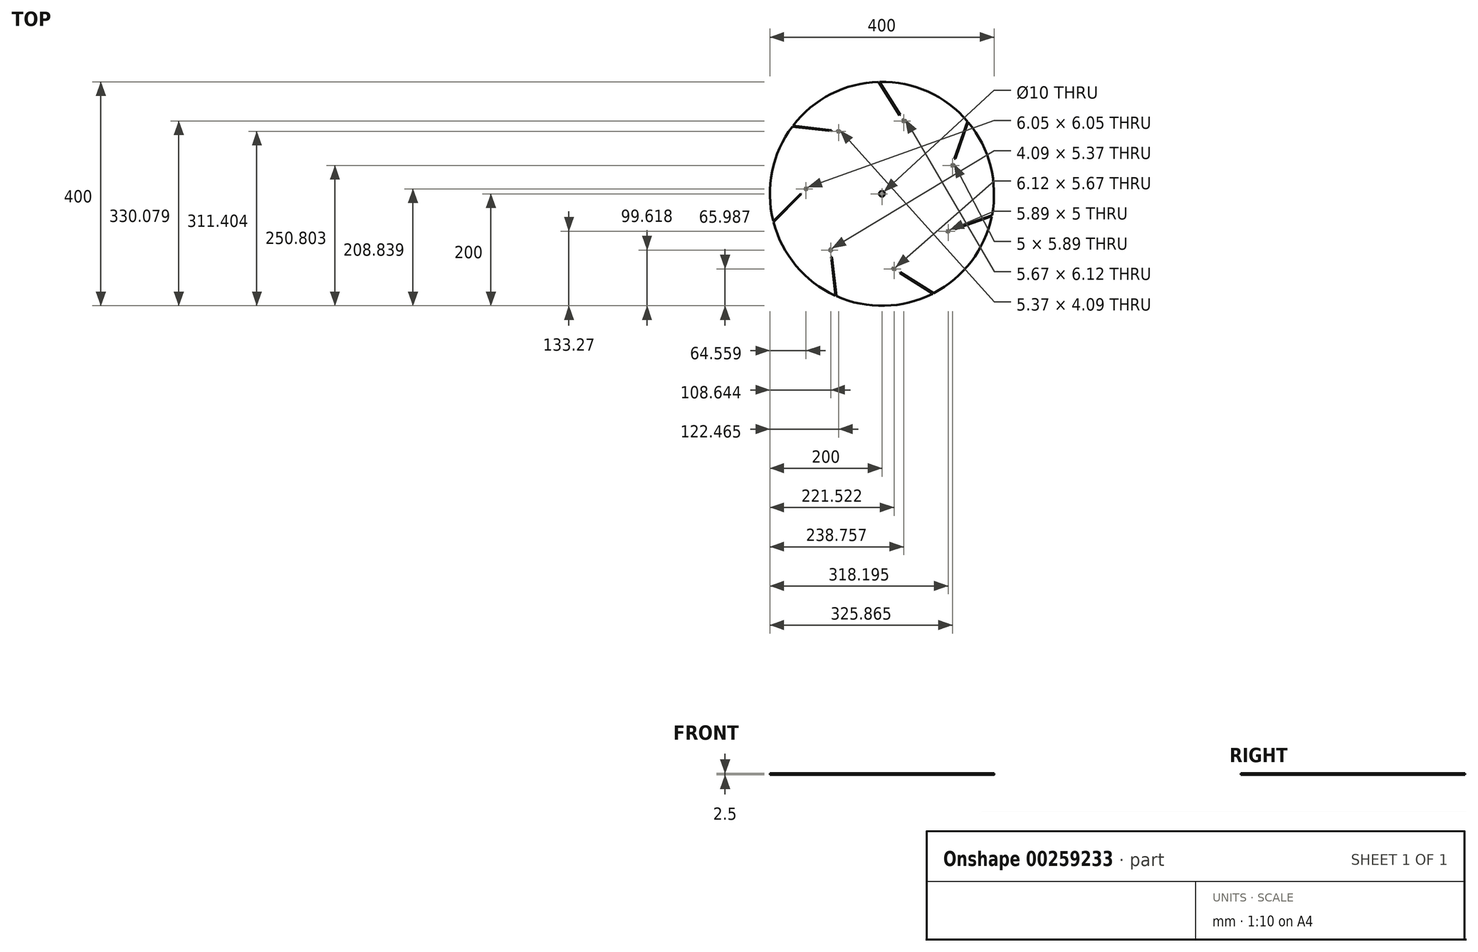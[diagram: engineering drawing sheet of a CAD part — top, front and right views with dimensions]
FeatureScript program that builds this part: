
annotation { "Feature Type Name" : "Feature", "Feature Type Description" : "" }
export const myFeature = defineFeature(function(context is Context, id is Id, definition is map)
    precondition{}
    {
        {
            var Q0;
            Q0=qCreatedBy(makeId("Top.planeOp"),FACE);
            var sketch = newSketch(context, id + "F0", { "sketchPlane" : qUnion([Q0])});
            skLineSegment(sketch, "E0", {"start": v(40, 0) * mm, "end": v(-285.91, 0) * mm, "construction": true});
            skCircle(sketch, "E1", {"center": v(0, 0) * mm, "radius": 70 * mm, "construction": true});
            skLineSegment(sketch, "E2", {"start": v(-49.5, -49.5) * mm, "end": v(49.5, 49.5) * mm, "construction": true});
            skLineSegment(sketch, "E3", {"start": v(-49.5, -49.5) * mm, "end": v(-221.75, -49.5) * mm, "construction": true});
            skLineSegment(sketch, "E4", {"start": v(-195.13, -50.85) * mm, "end": v(-94.78, 49.5) * mm, "construction": true});
            skPoint(sketch, "E5", {"position": v(-144.28, 0) * mm});
            skPoint(sketch, "E6", {"position": v(-193.78, -49.5) * mm});
            skCircle(sketch, "E7", {"center": v(-144.28, 0) * mm, "radius": 70 * mm, "construction": true});
            skCircle(sketch, "E8", {"center": v(-144.28, 0) * mm, "radius": 0.78 * mm, "construction": true});
            skLineSegment(sketch, "E9", {"start": v(-144.83, 0.55) * mm, "end": v(-193.64, -48.27) * mm});
            skLineSegment(sketch, "E10.trimOffspring", {"start": v(-143.73, -0.55) * mm, "end": v(-193.55, -50.37) * mm});
            skLineSegment(sketch, "E11", {"start": v(-144.83, 0.55) * mm, "end": v(-143.73, -0.55) * mm});
            skLineSegment(sketch, "E12", {"start": v(-138.46, 8.33) * mm, "end": v(-137.2, 7.07) * mm});
            skLineSegment(sketch, "E13", {"start": v(-134.93, 11.86) * mm, "end": v(-133.67, 10.6) * mm});
            skLineSegment(sketch, "E14", {"start": v(-134.93, 11.86) * mm, "end": v(-138.46, 8.33) * mm});
            skLineSegment(sketch, "E15.MirrorCS", {"start": v(-132.42, 9.35) * mm, "end": v(-133.67, 10.6) * mm});
            skLineSegment(sketch, "E16.MirrorCS", {"start": v(-135.95, 5.82) * mm, "end": v(-137.2, 7.07) * mm});
            skLineSegment(sketch, "E17.MirrorCS", {"start": v(-132.42, 9.35) * mm, "end": v(-135.95, 5.82) * mm});
            skCircle(sketch, "E18", {"center": v(0, 0) * mm, "radius": 5 * mm});
            skArc(sketch, "E19", {"start": v(-193.55, -50.37) * mm, "mid": v(-153.27, -128.48) * mm, "end": v(-83.4, -181.78) * mm});
            skCircle(sketch, "E20", {"center": v(-194, -48.62) * mm, "radius": 0.5 * mm, "construction": true});
            skLineSegment(sketch, "E21", {"start": v(-194.12, -48.14) * mm, "end": v(-193.64, -48.27) * mm});
            skLineSegment(sketch, "E22.1.2", {"start": v(-89.19, -112.72) * mm, "end": v(-81.3, -182.73) * mm});
            skLineSegment(sketch, "E22.1.3", {"start": v(-90.73, -112.9) * mm, "end": v(-83, -181.5) * mm});
            skPoint(sketch, "E22.1.4", {"position": v(-89.96, -112.8) * mm});
            skLineSegment(sketch, "E22.1.6", {"start": v(-89.87, -97.7) * mm, "end": v(-89.31, -102.67) * mm});
            skLineSegment(sketch, "E22.1.7", {"start": v(-93.4, -98.1) * mm, "end": v(-91.64, -97.9) * mm});
            skLineSegment(sketch, "E22.1.8", {"start": v(-89.87, -97.7) * mm, "end": v(-91.64, -97.9) * mm});
            skLineSegment(sketch, "E22.1.9", {"start": v(-89.31, -102.67) * mm, "end": v(-91.08, -102.87) * mm});
            skLineSegment(sketch, "E22.1.10", {"start": v(-93.4, -98.1) * mm, "end": v(-92.84, -103.06) * mm});
            skLineSegment(sketch, "E22.1.11", {"start": v(-92.84, -103.06) * mm, "end": v(-91.08, -102.87) * mm});
            skCircle(sketch, "E22.1.12", {"center": v(-89.96, -112.8) * mm, "radius": 0.78 * mm, "construction": true});
            skLineSegment(sketch, "E22.1.13", {"start": v(-90.73, -112.9) * mm, "end": v(-89.19, -112.72) * mm});
            skLineSegment(sketch, "E22.1.14", {"start": v(-83.4, -181.78) * mm, "end": v(-83, -181.5) * mm});
            skLineSegment(sketch, "E22.2.2", {"start": v(32.52, -140) * mm, "end": v(92.18, -177.5) * mm});
            skLineSegment(sketch, "E22.2.3", {"start": v(31.7, -141.32) * mm, "end": v(90.15, -178.05) * mm});
            skPoint(sketch, "E22.2.4", {"position": v(32.1, -140.66) * mm});
            skLineSegment(sketch, "E22.2.6", {"start": v(20.35, -131.18) * mm, "end": v(24.58, -133.84) * mm});
            skLineSegment(sketch, "E22.2.7", {"start": v(18.46, -134.19) * mm, "end": v(19.4, -132.68) * mm});
            skLineSegment(sketch, "E22.2.8", {"start": v(20.35, -131.18) * mm, "end": v(19.4, -132.68) * mm});
            skLineSegment(sketch, "E22.2.9", {"start": v(24.58, -133.84) * mm, "end": v(23.64, -135.34) * mm});
            skLineSegment(sketch, "E22.2.10", {"start": v(18.46, -134.19) * mm, "end": v(22.7, -136.85) * mm});
            skLineSegment(sketch, "E22.2.11", {"start": v(22.7, -136.85) * mm, "end": v(23.64, -135.34) * mm});
            skCircle(sketch, "E22.2.12", {"center": v(32.1, -140.66) * mm, "radius": 0.78 * mm, "construction": true});
            skLineSegment(sketch, "E22.2.13", {"start": v(31.7, -141.32) * mm, "end": v(32.52, -140) * mm});
            skLineSegment(sketch, "E22.2.14", {"start": v(90.13, -178.54) * mm, "end": v(90.15, -178.05) * mm});
            skLineSegment(sketch, "E22.3.2", {"start": v(129.74, -61.87) * mm, "end": v(196.24, -38.6) * mm});
            skLineSegment(sketch, "E22.3.3", {"start": v(130.25, -63.33) * mm, "end": v(195.41, -40.53) * mm});
            skPoint(sketch, "E22.3.4", {"position": v(130, -62.6) * mm});
            skLineSegment(sketch, "E22.3.6", {"start": v(115.25, -65.88) * mm, "end": v(119.97, -64.23) * mm});
            skLineSegment(sketch, "E22.3.7", {"start": v(116.42, -69.23) * mm, "end": v(115.84, -67.56) * mm});
            skLineSegment(sketch, "E22.3.8", {"start": v(115.25, -65.88) * mm, "end": v(115.84, -67.56) * mm});
            skLineSegment(sketch, "E22.3.9", {"start": v(119.97, -64.23) * mm, "end": v(120.55, -65.9) * mm});
            skLineSegment(sketch, "E22.3.10", {"start": v(116.42, -69.23) * mm, "end": v(121.14, -67.58) * mm});
            skLineSegment(sketch, "E22.3.11", {"start": v(121.14, -67.58) * mm, "end": v(120.55, -65.9) * mm});
            skCircle(sketch, "E22.3.12", {"center": v(130, -62.6) * mm, "radius": 0.78 * mm, "construction": true});
            skLineSegment(sketch, "E22.3.13", {"start": v(130.25, -63.33) * mm, "end": v(129.74, -61.87) * mm});
            skLineSegment(sketch, "E22.3.14", {"start": v(195.78, -40.86) * mm, "end": v(195.41, -40.53) * mm});
            skLineSegment(sketch, "E22.4.2", {"start": v(129.26, 62.86) * mm, "end": v(152.53, 129.36) * mm});
            skLineSegment(sketch, "E22.4.3", {"start": v(130.73, 62.35) * mm, "end": v(153.53, 127.5) * mm});
            skPoint(sketch, "E22.4.4", {"position": v(130, 62.6) * mm});
            skLineSegment(sketch, "E22.4.6", {"start": v(123.36, 49.03) * mm, "end": v(125.02, 53.75) * mm});
            skLineSegment(sketch, "E22.4.7", {"start": v(126.71, 47.86) * mm, "end": v(125.04, 48.44) * mm});
            skLineSegment(sketch, "E22.4.8", {"start": v(123.36, 49.03) * mm, "end": v(125.04, 48.44) * mm});
            skLineSegment(sketch, "E22.4.9", {"start": v(125.02, 53.75) * mm, "end": v(126.7, 53.16) * mm});
            skLineSegment(sketch, "E22.4.10", {"start": v(126.71, 47.86) * mm, "end": v(128.37, 52.58) * mm});
            skLineSegment(sketch, "E22.4.11", {"start": v(128.37, 52.58) * mm, "end": v(126.7, 53.16) * mm});
            skCircle(sketch, "E22.4.12", {"center": v(130, 62.6) * mm, "radius": 0.78 * mm, "construction": true});
            skLineSegment(sketch, "E22.4.13", {"start": v(130.73, 62.35) * mm, "end": v(129.26, 62.86) * mm});
            skLineSegment(sketch, "E22.4.14", {"start": v(154.01, 127.6) * mm, "end": v(153.53, 127.5) * mm});
            skLineSegment(sketch, "E22.5.2", {"start": v(31.45, 140.25) * mm, "end": v(-6.03, 199.9) * mm});
            skLineSegment(sketch, "E22.5.3", {"start": v(32.76, 141.08) * mm, "end": v(-3.97, 199.53) * mm});
            skPoint(sketch, "E22.5.4", {"position": v(32.1, 140.66) * mm});
            skLineSegment(sketch, "E22.5.6", {"start": v(38.58, 127.02) * mm, "end": v(35.92, 131.25) * mm});
            skLineSegment(sketch, "E22.5.7", {"start": v(41.59, 128.9) * mm, "end": v(40.09, 127.96) * mm});
            skLineSegment(sketch, "E22.5.8", {"start": v(38.58, 127.02) * mm, "end": v(40.09, 127.96) * mm});
            skLineSegment(sketch, "E22.5.9", {"start": v(35.92, 131.25) * mm, "end": v(37.43, 132.2) * mm});
            skLineSegment(sketch, "E22.5.10", {"start": v(41.59, 128.9) * mm, "end": v(38.93, 133.14) * mm});
            skLineSegment(sketch, "E22.5.11", {"start": v(38.93, 133.14) * mm, "end": v(37.43, 132.2) * mm});
            skCircle(sketch, "E22.5.12", {"center": v(32.1, 140.66) * mm, "radius": 0.78 * mm, "construction": true});
            skLineSegment(sketch, "E22.5.13", {"start": v(32.76, 141.08) * mm, "end": v(31.45, 140.25) * mm});
            skLineSegment(sketch, "E22.5.14", {"start": v(-3.73, 199.97) * mm, "end": v(-3.97, 199.53) * mm});
            skLineSegment(sketch, "E22.6.2", {"start": v(-90.04, 112.03) * mm, "end": v(-160.06, 119.92) * mm});
            skLineSegment(sketch, "E22.6.3", {"start": v(-89.87, 113.57) * mm, "end": v(-158.47, 121.3) * mm});
            skPoint(sketch, "E22.6.4", {"position": v(-89.96, 112.8) * mm});
            skLineSegment(sketch, "E22.6.6", {"start": v(-75.25, 109.36) * mm, "end": v(-80.22, 109.92) * mm});
            skLineSegment(sketch, "E22.6.7", {"start": v(-74.85, 112.89) * mm, "end": v(-75.05, 111.12) * mm});
            skLineSegment(sketch, "E22.6.8", {"start": v(-75.25, 109.36) * mm, "end": v(-75.05, 111.12) * mm});
            skLineSegment(sketch, "E22.6.9", {"start": v(-80.22, 109.92) * mm, "end": v(-80.02, 111.68) * mm});
            skLineSegment(sketch, "E22.6.10", {"start": v(-74.85, 112.89) * mm, "end": v(-79.82, 113.45) * mm});
            skLineSegment(sketch, "E22.6.11", {"start": v(-79.82, 113.45) * mm, "end": v(-80.02, 111.68) * mm});
            skCircle(sketch, "E22.6.12", {"center": v(-89.96, 112.8) * mm, "radius": 0.78 * mm, "construction": true});
            skLineSegment(sketch, "E22.6.13", {"start": v(-89.87, 113.57) * mm, "end": v(-90.04, 112.03) * mm});
            skLineSegment(sketch, "E22.6.14", {"start": v(-158.67, 121.76) * mm, "end": v(-158.47, 121.3) * mm});
            skArc(sketch, "E23.trimOffspring", {"start": v(-160.06, 119.92) * mm, "mid": v(-196.01, 39.73) * mm, "end": v(-194.12, -48.14) * mm});
            skArc(sketch, "E24.trimOffspring", {"start": v(-6.03, 199.9) * mm, "mid": v(-91.15, 178.02) * mm, "end": v(-158.67, 121.76) * mm});
            skArc(sketch, "E25.trimOffspring", {"start": v(152.53, 129.36) * mm, "mid": v(82.35, 182.26) * mm, "end": v(-3.73, 199.97) * mm});
            skArc(sketch, "E26.trimOffspring", {"start": v(196.24, -38.6) * mm, "mid": v(193.84, 49.25) * mm, "end": v(154.01, 127.6) * mm});
            skArc(sketch, "E27.trimOffspring", {"start": v(92.18, -177.5) * mm, "mid": v(159.37, -120.84) * mm, "end": v(195.78, -40.86) * mm});
            skArc(sketch, "E28.trimOffspring", {"start": v(-81.3, -182.73) * mm, "mid": v(4.89, -199.94) * mm, "end": v(90.13, -178.54) * mm});
            skSolve(sketch);
        }
        {
            var Q0;
            Q0=qSketchRegion(id+"F0",true);
            extrude(context, id + "F1", {"entities" : qUnion([Q0]), "depth" : 1.25 * mm, "hasSecondDirection" : true, "secondDirectionOppositeDirection" : true, "secondDirectionDepth" : 1.25 * mm});
        }
    });
